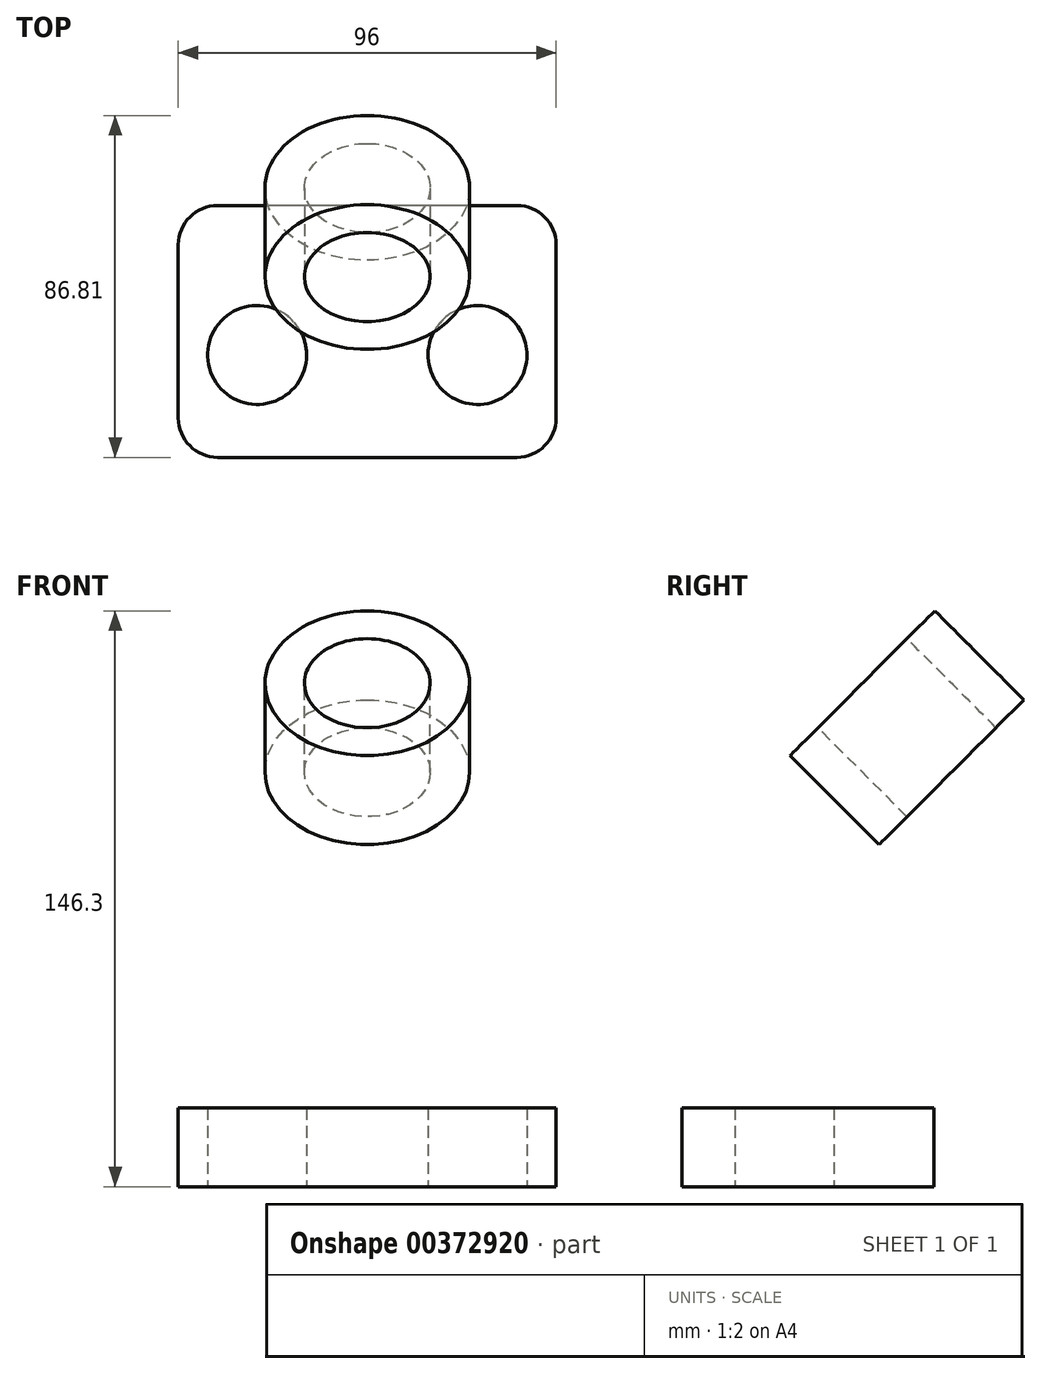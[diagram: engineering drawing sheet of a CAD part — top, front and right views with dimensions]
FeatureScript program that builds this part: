
annotation { "Feature Type Name" : "Feature", "Feature Type Description" : "" }
export const myFeature = defineFeature(function(context is Context, id is Id, definition is map)
    precondition{}
    {
        {
            var Q0;
            Q0=qCreatedBy(makeId("Top.planeOp"),FACE);
            var sketch = newSketch(context, id + "F0", { "sketchPlane" : qUnion([Q0])});
            skLineSegment(sketch, "E0.bottom", {"start": v(48, 32) * mm, "end": v(-48, 32) * mm});
            skLineSegment(sketch, "E0.top", {"start": v(48, -32) * mm, "end": v(-48, -32) * mm});
            skLineSegment(sketch, "E0.left", {"start": v(48, 32) * mm, "end": v(48, -32) * mm});
            skLineSegment(sketch, "E0.right", {"start": v(-48, 32) * mm, "end": v(-48, -32) * mm});
            skPoint(sketch, "E0.middle", {"position": v(0, 0) * mm});
            skSolve(sketch);
        }
        {
            var Q0;
            Q0=makeQuery(id+"F0.imprint","IMPRINT",FACE,{"disambiguationData":[TD([[makeQuery(id+"F0.imprint","IMPRINT",EDGE,{"derivedFrom":sQuery(id+"F0.wireOp",EDGE,"E0.bottom")}),1.0]])]});
            extrude(context, id + "F1", {"entities" : qUnion([Q0]), "depth" : 20 * mm});
        }
        {
            var Q0;
            Q0=makeQuery(id+"F1.opExtrude","SWEPT_EDGE",EDGE,{"disambiguationData":[OSD([sQuery(id+"F0.wireOp",EDGE,"E0.top"),sQuery(id+"F0.wireOp",EDGE,"E0.right")])]});
            var Q1;
            Q1=makeQuery(id+"F1.opExtrude","SWEPT_EDGE",EDGE,{"disambiguationData":[OSD([sQuery(id+"F0.wireOp",EDGE,"E0.top"),sQuery(id+"F0.wireOp",EDGE,"E0.left")])]});
            var Q2;
            Q2=makeQuery(id+"F1.opExtrude","SWEPT_EDGE",EDGE,{"disambiguationData":[OSD([sQuery(id+"F0.wireOp",EDGE,"E0.bottom"),sQuery(id+"F0.wireOp",EDGE,"E0.left")])]});
            var Q3;
            Q3=makeQuery(id+"F1.opExtrude","SWEPT_EDGE",EDGE,{"disambiguationData":[OSD([sQuery(id+"F0.wireOp",EDGE,"E0.bottom"),sQuery(id+"F0.wireOp",EDGE,"E0.right")])]});
            fillet(context, id + "F2", {"entities" : qUnion([Q0, Q1, Q2, Q3]), "radius" : 10 * mm, "tangentPropagation" : true, "allowEdgeOverflow" : false});
        }
        {
            var Q0;
            Q0=qCreatedBy(makeId("Top.planeOp"),FACE);
            var sketch = newSketch(context, id + "F3", { "sketchPlane" : qUnion([Q0])});
            skCircle(sketch, "E1", {"center": v(28, -6) * mm, "radius": 12.57 * mm});
            skCircle(sketch, "E2.MirrorC", {"center": v(-28, -6) * mm, "radius": 12.57 * mm});
            skSolve(sketch);
        }
        {
            var Q0;
            Q0 = qSketchRegion(id + "F3", true);
            extrude(context, id + "F4", {"entities" : qUnion([Q0]), "operationType" : NewBodyOperationType.REMOVE, "depth" : 25 * mm});
        }
        {
            var Q0;
            Q0=qCreatedBy(makeId("Right.planeOp"),FACE);
            var sketch = newSketch(context, id + "F5", { "sketchPlane" : qUnion([Q0])});
            skLineSegment(sketch, "E3", {"start": v(-88.15, 0) * mm, "end": v(-88.15, 146) * mm, "construction": true});
            skLineSegment(sketch, "E4", {"start": v(31.9, 0) * mm, "end": v(31.9, 146) * mm, "construction": true});
            skLineSegment(sketch, "E5", {"start": v(-88.15, 146) * mm, "end": v(31.9, 146) * mm, "construction": true});
            skLineSegment(sketch, "E6", {"start": v(2.84, 116.95) * mm, "end": v(67.38, 181.49) * mm});
            skSolve(sketch);
        }
        {
            var Q0;
            Q0=sQuery(id+"F5.wireOp",EDGE,"E6");
            extrude(context, id + "F6", {"bodyType" : ToolBodyType.SURFACE, "surfaceEntities" : qUnion([Q0]), "depth" : 25 * mm});
        }
        {
            var Q0;
            Q0=makeQuery(id+"F6.opExtrude","SWEPT_FACE",FACE,{"disambiguationData":[OSD([sQuery(id+"F5.wireOp",EDGE,"E6")])]});
            cPlane(context, id + "F7", {"entities" : qUnion([Q0]), "cplaneType" : CPlaneType.OFFSET, "offset" : 0 * mm, "oppositeDirection" : true, "width" : 150 * mm, "height" : 150 * mm});
        }
        {
            var Q0;
            Q0=qCreatedBy(id+"F7.planeOp",FACE);
            var sketch = newSketch(context, id + "F8", { "sketchPlane" : qUnion([Q0])});
            skCircle(sketch, "E7", {"center": v(0, 100.2) * mm, "radius": 16 * mm});
            skCircle(sketch, "E8", {"center": v(0, 100.2) * mm, "radius": 26 * mm});
            skSolve(sketch);
        }
        {
            var Q0;
            Q0=makeQuery(id+"F8.imprint","IMPRINT",FACE,{"disambiguationData":[TD([[makeQuery(id+"F8.imprint","IMPRINT",EDGE,{"derivedFrom":sQuery(id+"F8.wireOp",EDGE,"E7")}),-1.0]])]});
            extrude(context, id + "F9", {"entities" : qUnion([Q0]), "depth" : 32 * mm});
        }
    });
